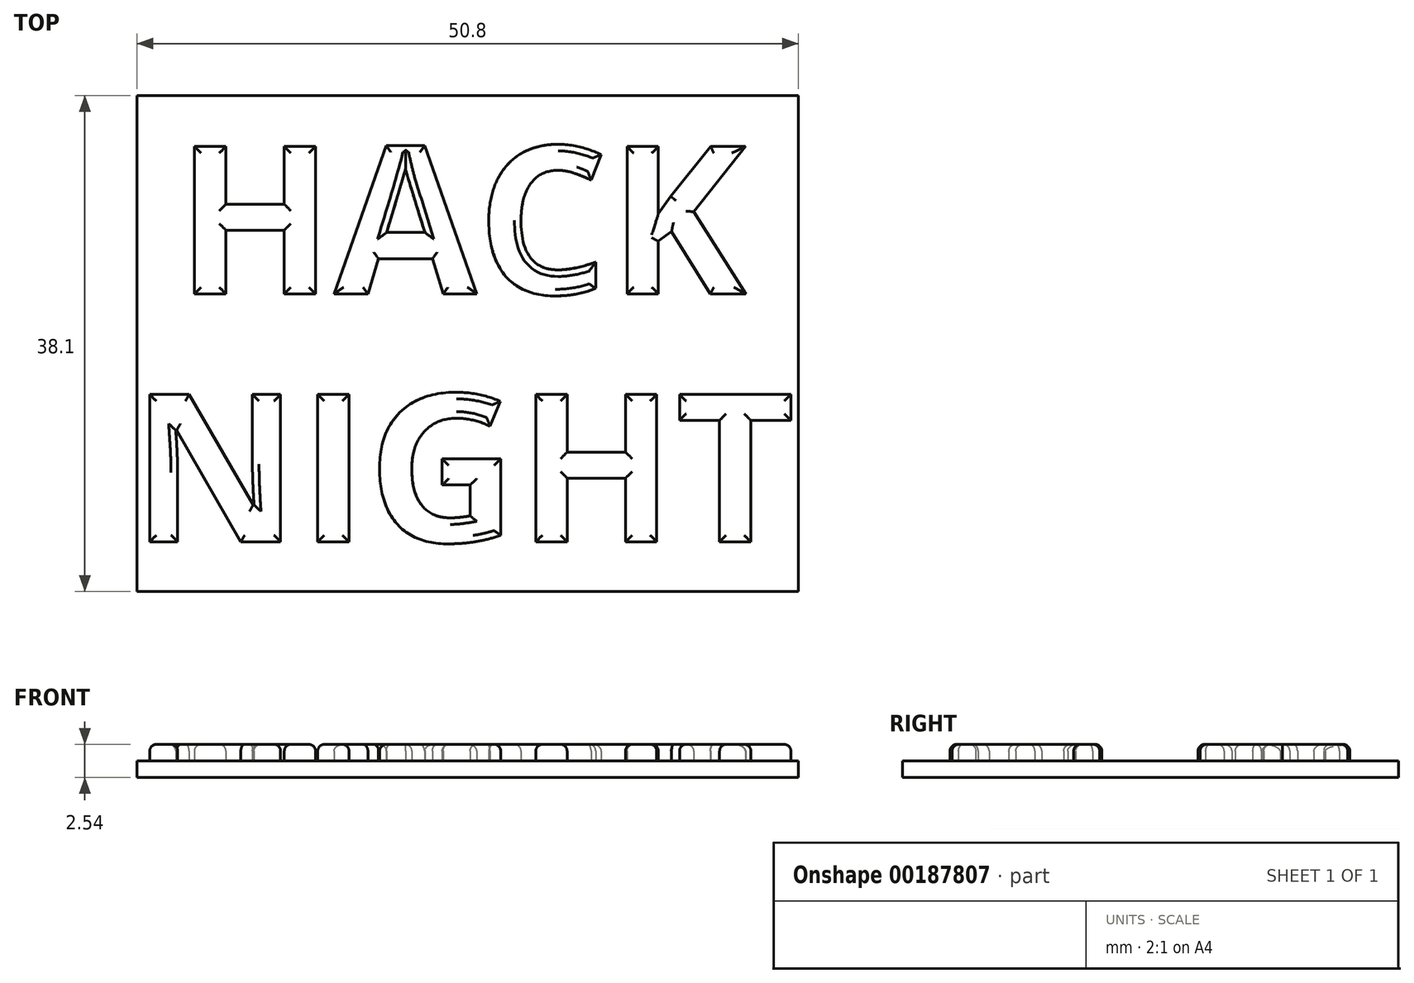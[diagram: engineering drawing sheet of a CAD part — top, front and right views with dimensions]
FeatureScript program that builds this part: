
annotation { "Feature Type Name" : "Feature", "Feature Type Description" : "" }
export const myFeature = defineFeature(function(context is Context, id is Id, definition is map)
    precondition{}
    {
        {
            var Q0;
            Q0=qCreatedBy(makeId("Top.planeOp"),FACE);
            var sketch = newSketch(context, id + "F0", { "sketchPlane" : qUnion([Q0])});
            skText(sketch, "E0", { "text": "HACK", "fontName": "OpenSans-Bold.ttf"});
            skText(sketch, "E1", { "text": "NIGHT", "fontName": "OpenSans-Bold.ttf"});
            skLineSegment(sketch, "E2.bottom", {"start": v(0, -19.05) * mm, "end": v(50.8, -19.05) * mm, "construction": true});
            skLineSegment(sketch, "E2.top", {"start": v(0, 19.05) * mm, "end": v(50.8, 19.05) * mm, "construction": true});
            skLineSegment(sketch, "E2.right", {"start": v(50.8, -19.05) * mm, "end": v(50.8, 19.05) * mm, "construction": true});
            skLineSegment(sketch, "E3", {"start": v(4.3, 3.8) * mm, "end": v(4.3, -3.8) * mm, "construction": true});
            skPoint(sketch, "E4", {"position": v(4.3, 0) * mm});
            skPoint(sketch, "E5", {"position": v(25.4, 19.05) * mm});
            skLineSegment(sketch, "E6", {"start": v(0, 19.05) * mm, "end": v(0, -19.05) * mm, "construction": true});
            skLineSegment(sketch, "E7", {"start": v(3, 15.24) * mm, "end": v(3, 19.05) * mm, "construction": true});
            skLineSegment(sketch, "E8", {"start": v(3, 3.8) * mm, "end": v(3, 0) * mm, "construction": true});
            const initialGuessF0  = {"E0": [0.003, 0.00381, 1, 0, 0.01143], "E1": [-0.00045, -0.01524, 1, 0, 0.01143]};
            skSetInitialGuess(sketch, initialGuessF0);
            skSolve(sketch);
        }
        {
            var Q0;
            Q0=qCreatedBy(makeId("Top.planeOp"),FACE);
            var sketch = newSketch(context, id + "F1", { "sketchPlane" : qUnion([Q0])});
            skLineSegment(sketch, "E9.bottom", {"start": v(0, -19.05) * mm, "end": v(50.8, -19.05) * mm});
            skLineSegment(sketch, "E9.top", {"start": v(0, 19.05) * mm, "end": v(50.8, 19.05) * mm});
            skLineSegment(sketch, "E9.left", {"start": v(0, -19.05) * mm, "end": v(0, 19.05) * mm});
            skLineSegment(sketch, "E9.right", {"start": v(50.8, -19.05) * mm, "end": v(50.8, 19.05) * mm});
            skSolve(sketch);
        }
        {
            var Q0;
            Q0 = qSketchRegion(id + "F1", true);
            extrude(context, id + "F2", {"entities" : qUnion([Q0]), "oppositeDirection" : true, "depth" : 1.27 * mm});
        }
        {
            var Q0;
            Q0 = qSketchRegion(id + "F0", true);
            extrude(context, id + "F3", {"entities" : qUnion([Q0]), "operationType" : NewBodyOperationType.ADD, "depth" : 1.27 * mm});
        }
        {
            var Q0;
            Q0=makeQuery(id+"F3.opExtrude","CAP_FACE",FACE,{"disambiguationData":[OSD([sQuery(id+"F0.wireOp",EDGE,"E0.sketch_text.stroke-0"),sQuery(id+"F0.wireOp",EDGE,"E0.sketch_text.stroke-1"),sQuery(id+"F0.wireOp",EDGE,"E0.sketch_text.stroke-2"),sQuery(id+"F0.wireOp",EDGE,"E0.sketch_text.stroke-3"),sQuery(id+"F0.wireOp",EDGE,"E0.sketch_text.stroke-4"),sQuery(id+"F0.wireOp",EDGE,"E0.sketch_text.stroke-5"),sQuery(id+"F0.wireOp",EDGE,"E0.sketch_text.stroke-6"),sQuery(id+"F0.wireOp",EDGE,"E0.sketch_text.stroke-7"),sQuery(id+"F0.wireOp",EDGE,"E0.sketch_text.stroke-8"),sQuery(id+"F0.wireOp",EDGE,"E0.sketch_text.stroke-9"),sQuery(id+"F0.wireOp",EDGE,"E0.sketch_text.stroke-10"),sQuery(id+"F0.wireOp",EDGE,"E0.sketch_text.stroke-11")])],"isStart":false});
            var Q1;
            Q1=makeQuery(id+"F3.opExtrude","CAP_FACE",FACE,{"disambiguationData":[OSD([sQuery(id+"F0.wireOp",EDGE,"E0.sketch_text.stroke-24"),sQuery(id+"F0.wireOp",EDGE,"E0.sketch_text.stroke-25"),sQuery(id+"F0.wireOp",EDGE,"E0.sketch_text.stroke-26"),sQuery(id+"F0.wireOp",EDGE,"E0.sketch_text.stroke-27"),sQuery(id+"F0.wireOp",EDGE,"E0.sketch_text.stroke-28"),sQuery(id+"F0.wireOp",EDGE,"E0.sketch_text.stroke-29"),sQuery(id+"F0.wireOp",EDGE,"E0.sketch_text.stroke-30"),sQuery(id+"F0.wireOp",EDGE,"E0.sketch_text.stroke-31"),sQuery(id+"F0.wireOp",EDGE,"E0.sketch_text.stroke-32"),sQuery(id+"F0.wireOp",EDGE,"E0.sketch_text.stroke-33"),sQuery(id+"F0.wireOp",EDGE,"E0.sketch_text.stroke-34"),sQuery(id+"F0.wireOp",EDGE,"E0.sketch_text.stroke-35"),sQuery(id+"F0.wireOp",EDGE,"E0.sketch_text.stroke-36"),sQuery(id+"F0.wireOp",EDGE,"E0.sketch_text.stroke-37"),sQuery(id+"F0.wireOp",EDGE,"E0.sketch_text.stroke-38")])],"isStart":false});
            var Q2;
            Q2=makeQuery(id+"F3.opExtrude","CAP_FACE",FACE,{"disambiguationData":[OSD([sQuery(id+"F0.wireOp",EDGE,"E0.sketch_text.stroke-39"),sQuery(id+"F0.wireOp",EDGE,"E0.sketch_text.stroke-40"),sQuery(id+"F0.wireOp",EDGE,"E0.sketch_text.stroke-41"),sQuery(id+"F0.wireOp",EDGE,"E0.sketch_text.stroke-42"),sQuery(id+"F0.wireOp",EDGE,"E0.sketch_text.stroke-43"),sQuery(id+"F0.wireOp",EDGE,"E0.sketch_text.stroke-44"),sQuery(id+"F0.wireOp",EDGE,"E0.sketch_text.stroke-45"),sQuery(id+"F0.wireOp",EDGE,"E0.sketch_text.stroke-46"),sQuery(id+"F0.wireOp",EDGE,"E0.sketch_text.stroke-47"),sQuery(id+"F0.wireOp",EDGE,"E0.sketch_text.stroke-48"),sQuery(id+"F0.wireOp",EDGE,"E0.sketch_text.stroke-49"),sQuery(id+"F0.wireOp",EDGE,"E0.sketch_text.stroke-50"),sQuery(id+"F0.wireOp",EDGE,"E0.sketch_text.stroke-51")])],"isStart":false});
            var Q3;
            Q3=makeQuery(id+"F3.opExtrude","CAP_FACE",FACE,{"disambiguationData":[OSD([sQuery(id+"F0.wireOp",EDGE,"E1.sketch_text.stroke-0"),sQuery(id+"F0.wireOp",EDGE,"E1.sketch_text.stroke-1"),sQuery(id+"F0.wireOp",EDGE,"E1.sketch_text.stroke-2"),sQuery(id+"F0.wireOp",EDGE,"E1.sketch_text.stroke-3"),sQuery(id+"F0.wireOp",EDGE,"E1.sketch_text.stroke-4"),sQuery(id+"F0.wireOp",EDGE,"E1.sketch_text.stroke-5"),sQuery(id+"F0.wireOp",EDGE,"E1.sketch_text.stroke-6"),sQuery(id+"F0.wireOp",EDGE,"E1.sketch_text.stroke-7"),sQuery(id+"F0.wireOp",EDGE,"E1.sketch_text.stroke-8"),sQuery(id+"F0.wireOp",EDGE,"E1.sketch_text.stroke-9"),sQuery(id+"F0.wireOp",EDGE,"E1.sketch_text.stroke-10"),sQuery(id+"F0.wireOp",EDGE,"E1.sketch_text.stroke-11"),sQuery(id+"F0.wireOp",EDGE,"E1.sketch_text.stroke-12"),sQuery(id+"F0.wireOp",EDGE,"E1.sketch_text.stroke-13")])],"isStart":false});
            var Q4;
            Q4=makeQuery(id+"F3.opExtrude","CAP_FACE",FACE,{"disambiguationData":[OSD([sQuery(id+"F0.wireOp",EDGE,"E1.sketch_text.stroke-14"),sQuery(id+"F0.wireOp",EDGE,"E1.sketch_text.stroke-15"),sQuery(id+"F0.wireOp",EDGE,"E1.sketch_text.stroke-16"),sQuery(id+"F0.wireOp",EDGE,"E1.sketch_text.stroke-17")])],"isStart":false});
            var Q5;
            Q5=makeQuery(id+"F3.opExtrude","CAP_FACE",FACE,{"disambiguationData":[OSD([sQuery(id+"F0.wireOp",EDGE,"E1.sketch_text.stroke-18"),sQuery(id+"F0.wireOp",EDGE,"E1.sketch_text.stroke-19"),sQuery(id+"F0.wireOp",EDGE,"E1.sketch_text.stroke-20"),sQuery(id+"F0.wireOp",EDGE,"E1.sketch_text.stroke-21"),sQuery(id+"F0.wireOp",EDGE,"E1.sketch_text.stroke-22"),sQuery(id+"F0.wireOp",EDGE,"E1.sketch_text.stroke-23"),sQuery(id+"F0.wireOp",EDGE,"E1.sketch_text.stroke-24"),sQuery(id+"F0.wireOp",EDGE,"E1.sketch_text.stroke-25"),sQuery(id+"F0.wireOp",EDGE,"E1.sketch_text.stroke-26"),sQuery(id+"F0.wireOp",EDGE,"E1.sketch_text.stroke-27"),sQuery(id+"F0.wireOp",EDGE,"E1.sketch_text.stroke-28"),sQuery(id+"F0.wireOp",EDGE,"E1.sketch_text.stroke-29"),sQuery(id+"F0.wireOp",EDGE,"E1.sketch_text.stroke-30"),sQuery(id+"F0.wireOp",EDGE,"E1.sketch_text.stroke-31"),sQuery(id+"F0.wireOp",EDGE,"E1.sketch_text.stroke-32"),sQuery(id+"F0.wireOp",EDGE,"E1.sketch_text.stroke-33"),sQuery(id+"F0.wireOp",EDGE,"E1.sketch_text.stroke-34"),sQuery(id+"F0.wireOp",EDGE,"E1.sketch_text.stroke-35"),sQuery(id+"F0.wireOp",EDGE,"E1.sketch_text.stroke-36")])],"isStart":false});
            var Q6;
            Q6=makeQuery(id+"F3.opExtrude","CAP_FACE",FACE,{"disambiguationData":[OSD([sQuery(id+"F0.wireOp",EDGE,"E1.sketch_text.stroke-37"),sQuery(id+"F0.wireOp",EDGE,"E1.sketch_text.stroke-38"),sQuery(id+"F0.wireOp",EDGE,"E1.sketch_text.stroke-39"),sQuery(id+"F0.wireOp",EDGE,"E1.sketch_text.stroke-40"),sQuery(id+"F0.wireOp",EDGE,"E1.sketch_text.stroke-41"),sQuery(id+"F0.wireOp",EDGE,"E1.sketch_text.stroke-42"),sQuery(id+"F0.wireOp",EDGE,"E1.sketch_text.stroke-43"),sQuery(id+"F0.wireOp",EDGE,"E1.sketch_text.stroke-44"),sQuery(id+"F0.wireOp",EDGE,"E1.sketch_text.stroke-45"),sQuery(id+"F0.wireOp",EDGE,"E1.sketch_text.stroke-46"),sQuery(id+"F0.wireOp",EDGE,"E1.sketch_text.stroke-47"),sQuery(id+"F0.wireOp",EDGE,"E1.sketch_text.stroke-48")])],"isStart":false});
            var Q7;
            Q7=makeQuery(id+"F3.opExtrude","CAP_FACE",FACE,{"disambiguationData":[OSD([sQuery(id+"F0.wireOp",EDGE,"E1.sketch_text.stroke-49"),sQuery(id+"F0.wireOp",EDGE,"E1.sketch_text.stroke-50"),sQuery(id+"F0.wireOp",EDGE,"E1.sketch_text.stroke-51"),sQuery(id+"F0.wireOp",EDGE,"E1.sketch_text.stroke-52"),sQuery(id+"F0.wireOp",EDGE,"E1.sketch_text.stroke-53"),sQuery(id+"F0.wireOp",EDGE,"E1.sketch_text.stroke-54"),sQuery(id+"F0.wireOp",EDGE,"E1.sketch_text.stroke-55"),sQuery(id+"F0.wireOp",EDGE,"E1.sketch_text.stroke-56")])],"isStart":false});
            var Q8;
            Q8=makeQuery(id+"F3.opExtrude","CAP_FACE",FACE,{"disambiguationData":[OSD([sQuery(id+"F0.wireOp",EDGE,"E0.sketch_text.stroke-12"),sQuery(id+"F0.wireOp",EDGE,"E0.sketch_text.stroke-13"),sQuery(id+"F0.wireOp",EDGE,"E0.sketch_text.stroke-14"),sQuery(id+"F0.wireOp",EDGE,"E0.sketch_text.stroke-15"),sQuery(id+"F0.wireOp",EDGE,"E0.sketch_text.stroke-16"),sQuery(id+"F0.wireOp",EDGE,"E0.sketch_text.stroke-17"),sQuery(id+"F0.wireOp",EDGE,"E0.sketch_text.stroke-18"),sQuery(id+"F0.wireOp",EDGE,"E0.sketch_text.stroke-19"),sQuery(id+"F0.wireOp",EDGE,"E0.sketch_text.stroke-20"),sQuery(id+"F0.wireOp",EDGE,"E0.sketch_text.stroke-21"),sQuery(id+"F0.wireOp",EDGE,"E0.sketch_text.stroke-22"),sQuery(id+"F0.wireOp",EDGE,"E0.sketch_text.stroke-23")])],"isStart":false});
            fillet(context, id + "F4", {"entities" : qUnion([Q0, Q1, Q2, Q3, Q4, Q5, Q6, Q7, Q8]), "radius" : 0.5 * mm, "tangentPropagation" : true, "allowEdgeOverflow" : false});
        }
    });
